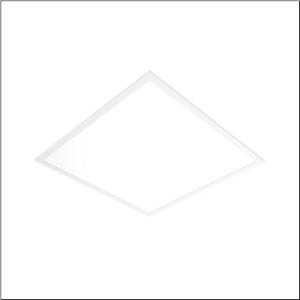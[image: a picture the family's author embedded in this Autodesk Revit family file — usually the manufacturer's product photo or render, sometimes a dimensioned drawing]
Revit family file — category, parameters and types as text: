
# Revit family: apollon_r__41_51mh11w72443_9aaa
name_source: partatom
category: Lighting Fixtures
units: mm (PartAtom-declared; Revit-internal decimal feet)

## family parameters
Cut with Voids When Loaded = No
Host = Face
Light Source = No
Part Type = Normal
Room Calculation Point = No
Round Connector Dimension = Use Diameter
Shared = No

## types (1)
- Apollon® 41 (1 x LED, 3700 lm, 28.5 W, 4000K)
    Apparent Load = 29 VA
    CIE Flux Codes = 61 87 97 100 100
    Color Rendering = 80
    Color Temperature = 4000K
    Default Elevation = 1800 mm
    Description = Apollon® 41, office luminaire, primary optical cover: prismatic diffuser, of PS, light emission: direct distribution, primary light characteristic: symmetric, installation type: lay-in mounting, LED, rated luminous flux: 3.700lm, luminous efficacy: 130lm/W, light colour: 840, colour temperature: 4000K, with terminal, 3-pole, mains connection: 220..240V, AC, 50/60Hz, housing, of aluminium section, traffic white (RAL 9016), module: M625, length: 620mm, width: 620mm, height: 40mm, housing upper side, of sheet steel, protection rating (complete): IP20, protection rating (lamp compartment, on room side): IP40, insulation class (complete): insulation class II (safety insulation), certification: CE, ENEC, permissible operating ambient temperature: -20..+40°C, packaging unit: 1 piece
    Height = 0 mm  [stored 0 ft]
    Lamp = 1 x LED
    Lamp Light Flux = 3700 lm
    Lamp Power = 28.5 W
    Lamp count = 1
    Length = 620 mm
    Luminous efficacy = 130 lm/W
    Manufacturer = Siteco
    ModVariant = No
    Model = 51MH11W72443
    Mounting Place = Ceiling
    Mounting Type = Recessed
    Number of Poles = 1
    OnlyDefault = Yes
    Power Factor = 1
    Product Name = Apollon® 41
    Product group = office luminaire | ceiling recessed
    ProductGroupID = 400
    Protection Class = Protection class II
    Protection Degree = IP 20
    RLX_Detail_Level = 1
    RLX_Emergency_Light_Flux = 0 lm
    RLX_Emergency_Type = 0
    RLX_Emergency_Type_DB = No
    RlxData = <blob elided: 12177 chars, md5=104b057e>
    Socket = socket
    Standby Power = 0 W
    System Light Flux = 3700 lm
    System Power = 29 W
    Type Comments = Product without accessories
    Type Image = l_1291024.jpg
    URL = http://relux.com
    VarID = ---
    Voltage = 0 V
    Weight = 0.00 kg
    Width = 620 mm

note: [stored X ft] marks values corroborated as IEEE doubles in the binary element streams (Revit-internal decimal feet)

## geometry (parser evidence)
native form markers: Sweep x10
no freeform markers — native parametric forms only
